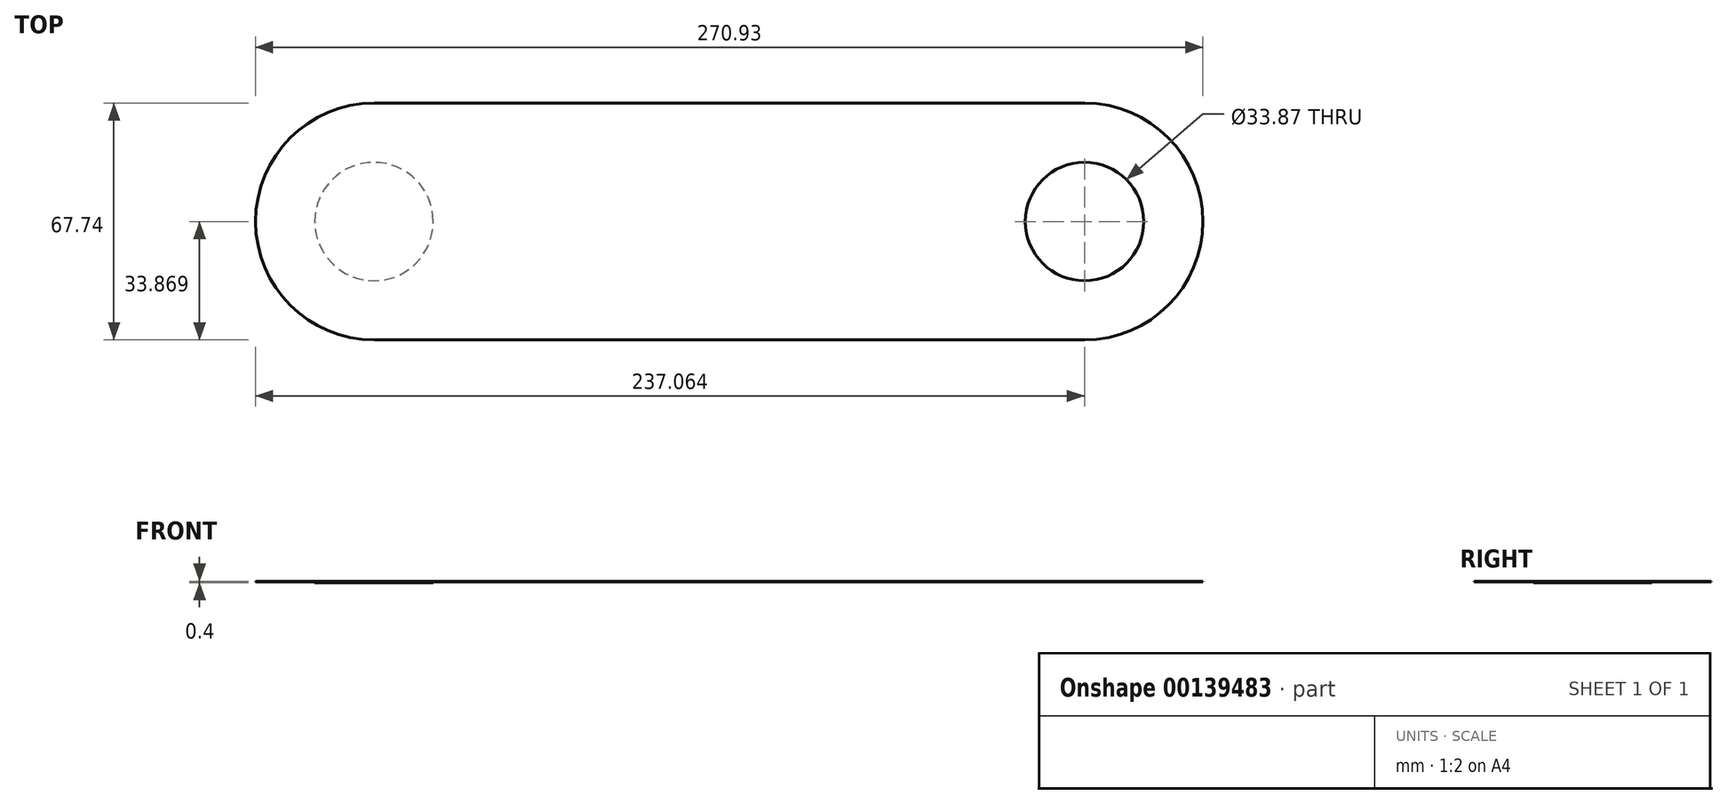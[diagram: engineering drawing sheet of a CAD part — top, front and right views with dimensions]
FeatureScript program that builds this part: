
annotation { "Feature Type Name" : "Feature", "Feature Type Description" : "" }
export const myFeature = defineFeature(function(context is Context, id is Id, definition is map)
    precondition{}
    {
        {
            assignVariable(context, id + "F0", {"name" : "Depth", "anyValue" : .2});
        }
        {
            var Q0;
            Q0=qCreatedBy(makeId("Top.planeOp"),FACE);
            var sketch = newSketch(context, id + "F1", { "sketchPlane" : qUnion([Q0])});
            skLineSegment(sketch, "E0.bottom", {"start": v(100.82, 20.2) * mm, "end": v(-102.38, 20.2) * mm});
            skLineSegment(sketch, "E0.top", {"start": v(100.82, -47.53) * mm, "end": v(-102.38, -47.53) * mm});
            skArc(sketch, "E1", {"start": v(100.82, 20.2) * mm, "mid": v(134.7, -13.66) * mm, "end": v(100.82, -47.53) * mm});
            skArc(sketch, "E2", {"start": v(-102.38, -47.53) * mm, "mid": v(-136.24, -13.66) * mm, "end": v(-102.38, 20.2) * mm});
            skSolve(sketch);
        }
        {
            var Q0;
            Q0=makeQuery(id+"F1.imprint","IMPRINT",FACE,{"disambiguationData":[TD([[makeQuery(id+"F1.imprint","IMPRINT",EDGE,{"derivedFrom":sQuery(id+"F1.wireOp",EDGE,"E0.bottom")}),1.0]])]});
            extrude(context, id + "F2", {"entities" : qUnion([Q0]), "depth" : (getVariable(context, 'Depth')) * mm});
        }
        {
            var Q0;
            Q0=makeQuery(id+"F2.opExtrude","CAP_FACE",FACE,{"disambiguationData":[OSD([sQuery(id+"F1.wireOp",EDGE,"E0.bottom"),sQuery(id+"F1.wireOp",EDGE,"E0.top"),sQuery(id+"F1.wireOp",EDGE,"E1"),sQuery(id+"F1.wireOp",EDGE,"E2")])],"isStart":true});
            var sketch = newSketch(context, id + "F3", { "sketchPlane" : qUnion([Q0])});
            skCircle(sketch, "E3", {"center": v(-102.38, 13.66) * mm, "radius": 16.93 * mm});
            skCircle(sketch, "E4", {"center": v(100.82, 13.66) * mm, "radius": 16.93 * mm});
            skSolve(sketch);
        }
        {
            var Q0;
            Q0=makeQuery(id+"F3.imprint","IMPRINT",FACE,{"disambiguationData":[TD([[makeQuery(id+"F3.imprint","IMPRINT",EDGE,{"derivedFrom":sQuery(id+"F3.wireOp",EDGE,"E3")}),1.0]])]});
            extrude(context, id + "F4", {"entities" : qUnion([Q0]), "operationType" : NewBodyOperationType.ADD, "depth" : (getVariable(context, 'Depth')) * mm});
        }
        {
            var Q0;
            Q0=makeQuery(id+"F3.imprint","IMPRINT",FACE,{"disambiguationData":[TD([[makeQuery(id+"F3.imprint","IMPRINT",EDGE,{"derivedFrom":sQuery(id+"F3.wireOp",EDGE,"E4")}),1.0]])]});
            extrude(context, id + "F5", {"entities" : qUnion([Q0]), "operationType" : NewBodyOperationType.REMOVE, "oppositeDirection" : true, "depth" : (getVariable(context, 'Depth')) * mm});
        }
    });
